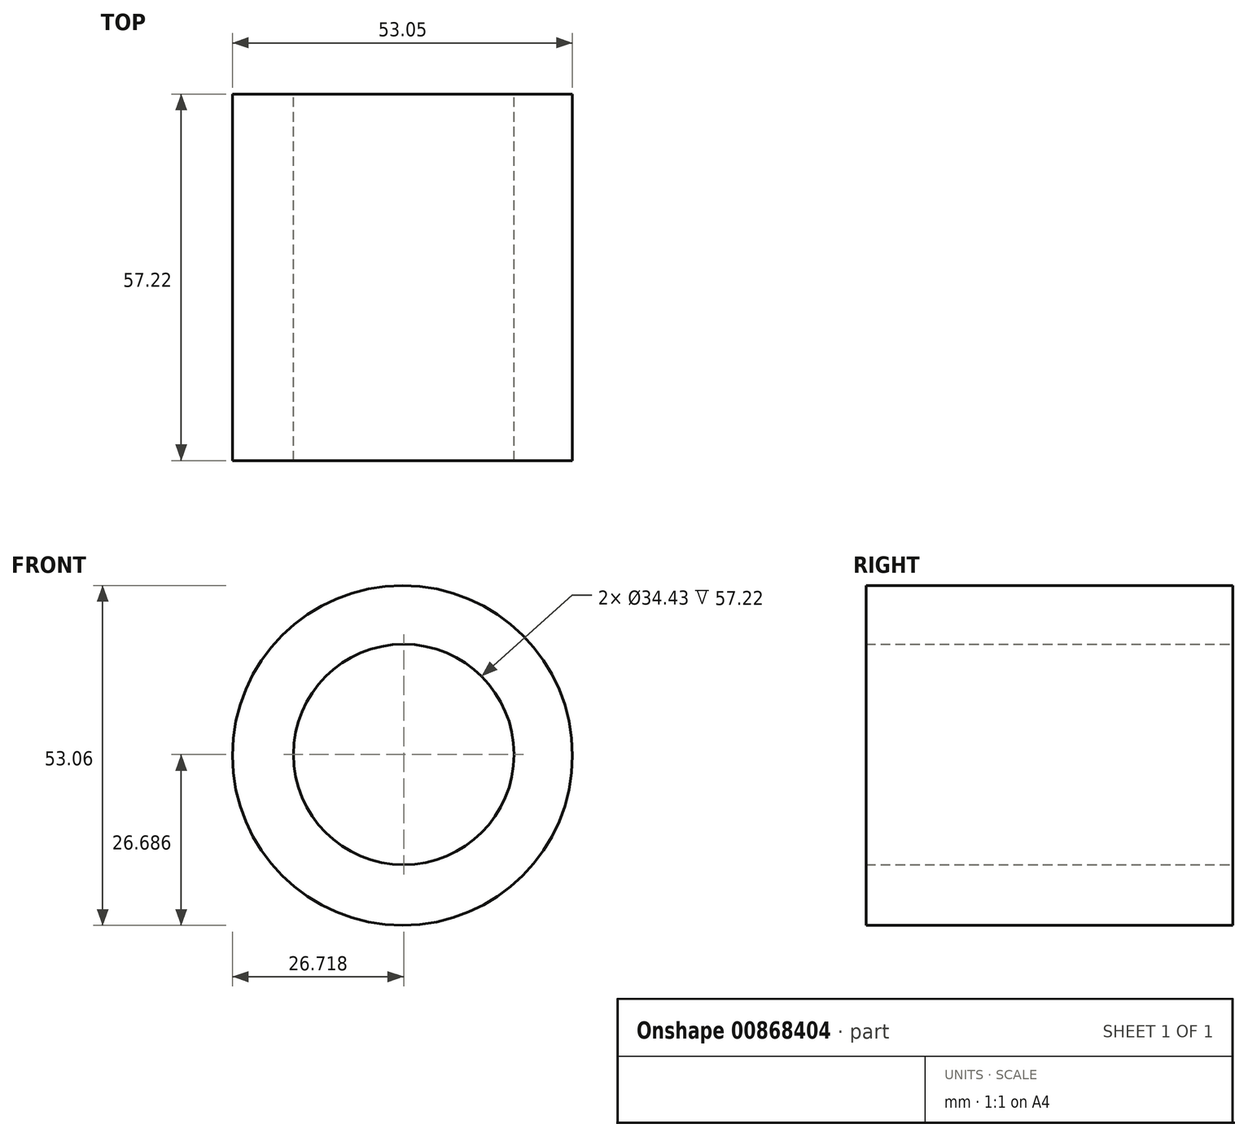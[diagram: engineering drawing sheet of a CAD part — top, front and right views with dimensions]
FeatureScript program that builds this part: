
annotation { "Feature Type Name" : "Feature", "Feature Type Description" : "" }
export const myFeature = defineFeature(function(context is Context, id is Id, definition is map)
    precondition{}
    {
        {
            var Q0;
            Q0=qCreatedBy(makeId("Front.planeOp"),FACE);
            var sketch = newSketch(context, id + "F0", { "sketchPlane" : qUnion([Q0])});
            skCircle(sketch, "E0", {"center": v(148.05, 0) * mm, "radius": 26.53 * mm});
            skCircle(sketch, "E1", {"center": v(148.24, 0.16) * mm, "radius": 17.21 * mm});
            skSolve(sketch);
        }
        {
            var Q0;
            Q0=makeQuery(id+"F0.imprint","IMPRINT",FACE,{"disambiguationData":[TD([[makeQuery(id+"F0.imprint","IMPRINT",EDGE,{"derivedFrom":sQuery(id+"F0.wireOp",EDGE,"E0")}),1.0]])]});
            extrude(context, id + "F1", {"entities" : qUnion([Q0]), "depth" : 57.22 * mm, "offsetDistance" : 25.4 * mm});
        }
    });
